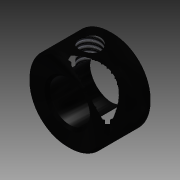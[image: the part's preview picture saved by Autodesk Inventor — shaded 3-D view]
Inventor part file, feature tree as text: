
AUTODESK INVENTOR PART (.ipt)
format: ipt  version: 2014 (Build 180170000, 170)  size: 112,128 bytes
history: native  units: in
note: dims shown in document units (in); Inventor stores cm internally (conversion verified against a paired STEP export)
features: sketch x3, extrude x2, chamfer x1, plane x1, hole x1
ambient origin geometry x8: Origin, YZ Plane, XZ Plane, XY Plane, X Axis, Y Axis, Z Axis, Center Point
bodies: Solid1 (feature_tree)
feature tree (8):
  extrude  "Extrusion1"  Depth=0.281in TaperAngle=0.0deg
  extrude  "Extrusion2"  Depth=0.125in TaperAngle=0.0deg
  chamfer  "Chamfer1"  Distance=0.125in Angle=45.0deg
  plane  "Work Plane1"
  hole  "Hole1"  [1 undecoded]
  sketch  "Sketch1"  dims[d0=0.5in d1=0.281in d2=0.0in]
  sketch  "Sketch2"  dims[d3=0.25in d4=0.281in d5=0.0in d6=0.0156in d7=0.125in d8=45.0deg]
  sketch  "Sketch3"  dims[d9=0.13in d10=0.75in d11=0.375in d12=0.25in d13=0.5635in d14=1.0in d15=0.8108in]
note: 1 required parameter value undecoded (feature->parameter linkage not recoverable at this tier; creation-order binding heuristic only, values carry confidence <= 0.55)
